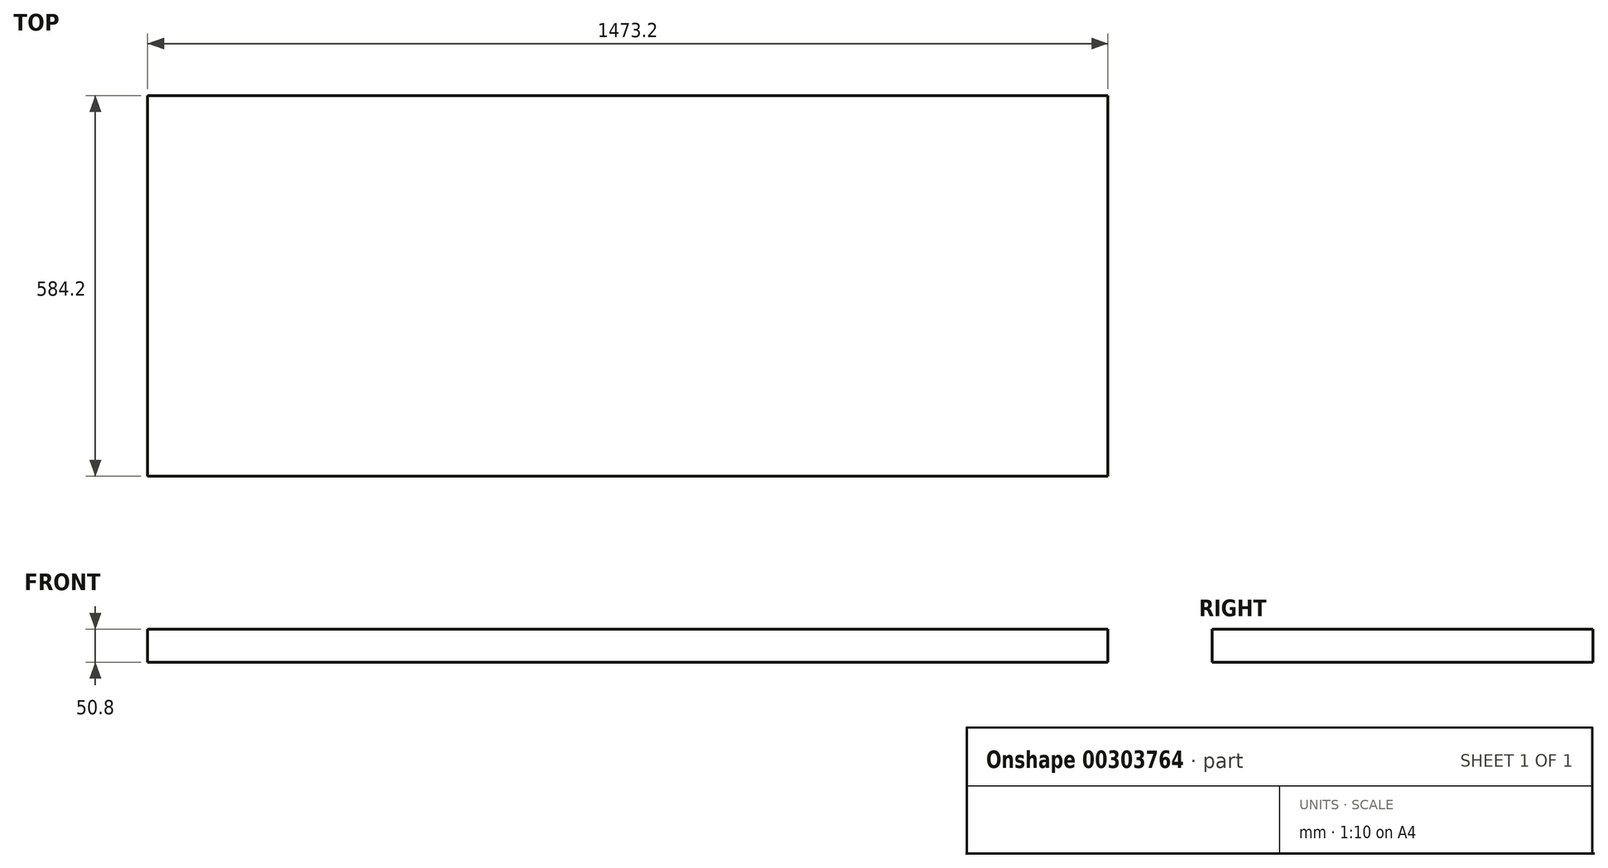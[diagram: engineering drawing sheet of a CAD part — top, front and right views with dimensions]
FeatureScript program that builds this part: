
annotation { "Feature Type Name" : "Feature", "Feature Type Description" : "" }
export const myFeature = defineFeature(function(context is Context, id is Id, definition is map)
    precondition{}
    {
        {
            var Q0;
            Q0=qCreatedBy(makeId("Top.planeOp"),FACE);
            var sketch = newSketch(context, id + "F0", { "sketchPlane" : qUnion([Q0])});
            skLineSegment(sketch, "E0.bottom", {"start": v(0, 0) * mm, "end": v(1473.2, 0) * mm});
            skLineSegment(sketch, "E0.top", {"start": v(0, 584.2) * mm, "end": v(1473.2, 584.2) * mm});
            skLineSegment(sketch, "E0.left", {"start": v(0, 0) * mm, "end": v(0, 584.2) * mm});
            skLineSegment(sketch, "E0.right", {"start": v(1473.2, 0) * mm, "end": v(1473.2, 584.2) * mm});
            skSolve(sketch);
        }
        {
            var Q0;
            Q0=makeQuery(id+"F0.imprint","IMPRINT",FACE,{"disambiguationData":[TD([[makeQuery(id+"F0.imprint","IMPRINT",EDGE,{"derivedFrom":sQuery(id+"F0.wireOp",EDGE,"E0.bottom")}),1.0]])]});
            extrude(context, id + "F1", {"entities" : qUnion([Q0]), "offsetDistance" : 25.4 * mm, "depth" : 50.8 * mm});
        }
    });
